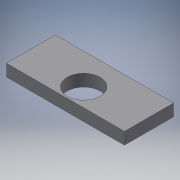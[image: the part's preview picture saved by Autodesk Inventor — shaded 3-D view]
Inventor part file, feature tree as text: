
AUTODESK INVENTOR PART (.ipt)
format: ipt  version: 2018 (Build 220112000, 112)  size: 114,176 bytes
history: native  units: mm
features: sketch x2, other x1, extrude x1, hole x1
ambient origin geometry x8: Origin, YZ Plane, XZ Plane, XY Plane, X Axis, Y Axis, Z Axis, Center Point
bodies: Body1 (feature_tree)
feature tree (5):
  other  "Sólido1"
  extrude  "Extrusão1"  Depth=52.0mm
  hole  "Furo1"  [1 undecoded]
  sketch  "Esboço1"  dims[d0=52.0mm d1=23.0mm]
  sketch  "Esboço2"  dims[d2=125.0mm d3=12.7mm d4=0.0mm d5=2.0mm d6=2.0mm d7=2.0mm d8=2.0mm d9=2.0mm d10=2.0mm d11=4.134mm d12=10.0mm d13=4.0mm d14=2.0mm d15=90.0deg d16=14.2mm d17=20.594885mm]
note: 1 required parameter value undecoded (feature->parameter linkage not recoverable at this tier; creation-order binding heuristic only, values carry confidence <= 0.55)
